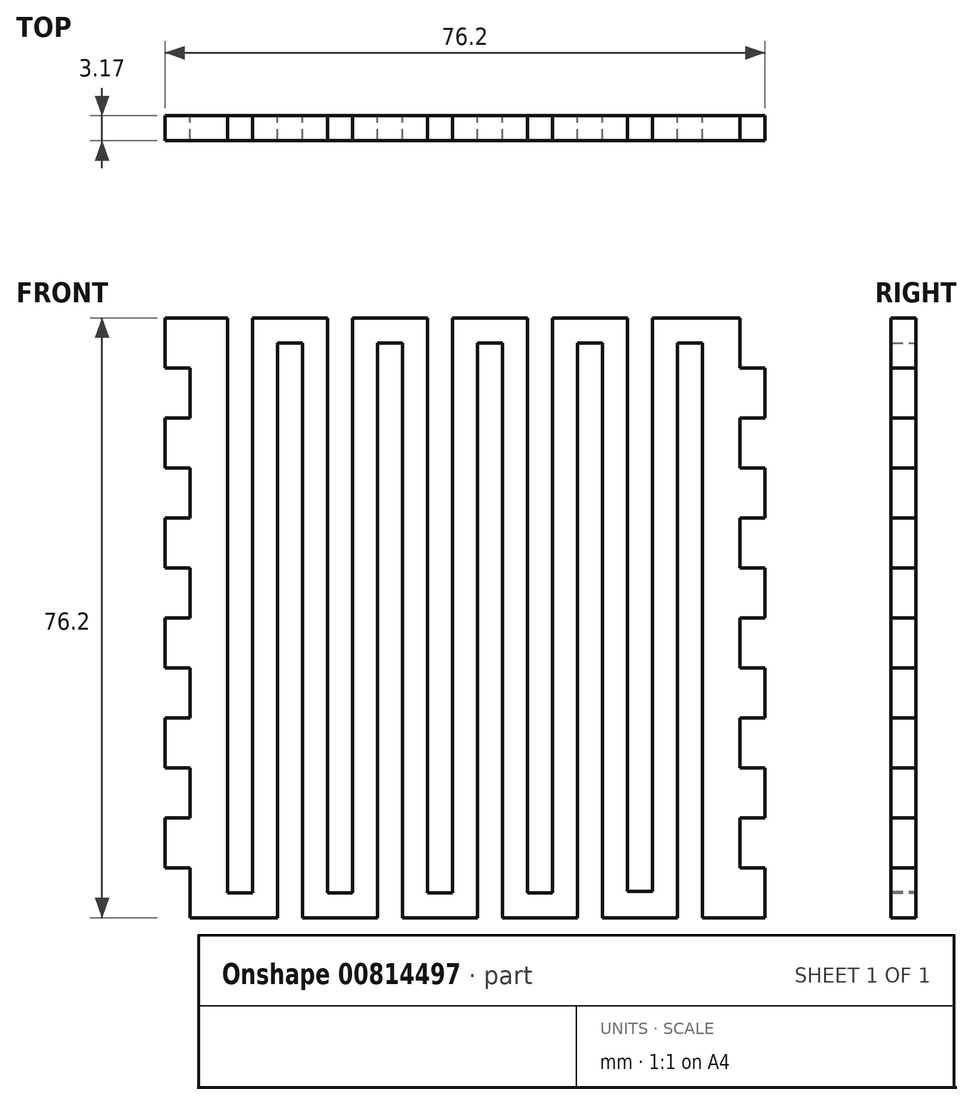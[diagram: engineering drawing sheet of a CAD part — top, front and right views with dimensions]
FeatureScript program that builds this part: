
annotation { "Feature Type Name" : "Feature", "Feature Type Description" : "" }
export const myFeature = defineFeature(function(context is Context, id is Id, definition is map)
    precondition{}
    {
        {
            var Q0;
            Q0=qCreatedBy(makeId("Front.planeOp"),FACE);
            var sketch = newSketch(context, id + "F0", { "sketchPlane" : qUnion([Q0])});
            skLineSegment(sketch, "E0.bottom", {"start": v(-38.1, 38.1) * mm, "end": v(38.1, 38.1) * mm});
            skLineSegment(sketch, "E0.top", {"start": v(-38.1, -38.1) * mm, "end": v(38.1, -38.1) * mm});
            skLineSegment(sketch, "E0.left", {"start": v(-38.1, 38.1) * mm, "end": v(-38.1, -38.1) * mm});
            skLineSegment(sketch, "E0.right", {"start": v(38.1, 38.1) * mm, "end": v(38.1, -38.1) * mm});
            skLineSegment(sketch, "E1.bottom", {"start": v(34.93, 38.1) * mm, "end": v(38.1, 38.1) * mm});
            skLineSegment(sketch, "E1.top", {"start": v(34.93, 31.75) * mm, "end": v(38.1, 31.75) * mm});
            skLineSegment(sketch, "E1.left", {"start": v(34.93, 38.1) * mm, "end": v(34.93, 31.75) * mm});
            skLineSegment(sketch, "E1.right", {"start": v(38.1, 38.1) * mm, "end": v(38.1, 31.75) * mm});
            skLineSegment(sketch, "E2.bottom", {"start": v(34.93, 25.4) * mm, "end": v(38.1, 25.4) * mm});
            skLineSegment(sketch, "E2.top", {"start": v(34.93, 19.05) * mm, "end": v(38.1, 19.05) * mm});
            skLineSegment(sketch, "E2.left", {"start": v(34.93, 25.4) * mm, "end": v(34.93, 19.05) * mm});
            skLineSegment(sketch, "E2.right", {"start": v(38.1, 25.4) * mm, "end": v(38.1, 19.05) * mm});
            skLineSegment(sketch, "E3.bottom", {"start": v(34.93, 12.7) * mm, "end": v(38.1, 12.7) * mm});
            skLineSegment(sketch, "E3.top", {"start": v(34.93, 6.35) * mm, "end": v(38.1, 6.35) * mm});
            skLineSegment(sketch, "E3.left", {"start": v(34.93, 12.7) * mm, "end": v(34.93, 6.35) * mm});
            skLineSegment(sketch, "E3.right", {"start": v(38.1, 12.7) * mm, "end": v(38.1, 6.35) * mm});
            skLineSegment(sketch, "E4.bottom", {"start": v(34.93, -12.7) * mm, "end": v(38.1, -12.7) * mm});
            skLineSegment(sketch, "E4.top", {"start": v(34.93, -19.05) * mm, "end": v(38.1, -19.05) * mm});
            skLineSegment(sketch, "E4.left", {"start": v(34.93, -12.7) * mm, "end": v(34.93, -19.05) * mm});
            skLineSegment(sketch, "E4.right", {"start": v(38.1, -12.7) * mm, "end": v(38.1, -19.05) * mm});
            skLineSegment(sketch, "E5.bottom", {"start": v(38.1, 0) * mm, "end": v(34.93, 0) * mm});
            skLineSegment(sketch, "E5.top", {"start": v(38.1, -6.35) * mm, "end": v(34.93, -6.35) * mm});
            skLineSegment(sketch, "E5.left", {"start": v(38.1, 0) * mm, "end": v(38.1, -6.35) * mm});
            skLineSegment(sketch, "E5.right", {"start": v(34.93, 0) * mm, "end": v(34.93, -6.35) * mm});
            skLineSegment(sketch, "E6.bottom", {"start": v(38.1, -25.4) * mm, "end": v(34.93, -25.4) * mm});
            skLineSegment(sketch, "E6.top", {"start": v(38.1, -31.75) * mm, "end": v(34.93, -31.75) * mm});
            skLineSegment(sketch, "E6.left", {"start": v(38.1, -25.4) * mm, "end": v(38.1, -31.75) * mm});
            skLineSegment(sketch, "E6.right", {"start": v(34.93, -25.4) * mm, "end": v(34.93, -31.75) * mm});
            skLineSegment(sketch, "E7.MirrorCS", {"start": v(-38.1, 12.7) * mm, "end": v(-38.1, 6.35) * mm});
            skLineSegment(sketch, "E8.MirrorCS", {"start": v(-38.1, -12.7) * mm, "end": v(-38.1, -19.05) * mm});
            skLineSegment(sketch, "E9.MirrorCS", {"start": v(-38.1, -25.4) * mm, "end": v(-38.1, -31.75) * mm});
            skLineSegment(sketch, "E10.MirrorCS", {"start": v(-38.1, 0) * mm, "end": v(-38.1, -6.35) * mm});
            skLineSegment(sketch, "E11.MirrorCS", {"start": v(-38.1, -31.75) * mm, "end": v(-34.93, -31.75) * mm});
            skLineSegment(sketch, "E12.MirrorCS", {"start": v(-34.93, -19.05) * mm, "end": v(-38.1, -19.05) * mm});
            skLineSegment(sketch, "E13.MirrorCS", {"start": v(-38.1, 38.1) * mm, "end": v(-38.1, 31.75) * mm});
            skLineSegment(sketch, "E14.MirrorCS", {"start": v(-34.93, 31.75) * mm, "end": v(-38.1, 31.75) * mm});
            skLineSegment(sketch, "E15.MirrorCS", {"start": v(-38.1, -6.35) * mm, "end": v(-34.93, -6.35) * mm});
            skLineSegment(sketch, "E16.MirrorCS", {"start": v(-34.93, 38.1) * mm, "end": v(-38.1, 38.1) * mm});
            skLineSegment(sketch, "E17.MirrorCS", {"start": v(-34.93, -12.7) * mm, "end": v(-38.1, -12.7) * mm});
            skLineSegment(sketch, "E18.MirrorCS", {"start": v(-38.1, 0) * mm, "end": v(-34.93, 0) * mm});
            skLineSegment(sketch, "E19.MirrorCS", {"start": v(-34.93, 12.7) * mm, "end": v(-38.1, 12.7) * mm});
            skLineSegment(sketch, "E20.MirrorCS", {"start": v(-38.1, 25.4) * mm, "end": v(-38.1, 19.05) * mm});
            skLineSegment(sketch, "E21.MirrorCS", {"start": v(-34.93, 6.35) * mm, "end": v(-38.1, 6.35) * mm});
            skLineSegment(sketch, "E22.MirrorCS", {"start": v(-34.93, 19.05) * mm, "end": v(-38.1, 19.05) * mm});
            skLineSegment(sketch, "E23.MirrorCS", {"start": v(-34.93, 25.4) * mm, "end": v(-38.1, 25.4) * mm});
            skLineSegment(sketch, "E24.MirrorCS", {"start": v(-38.1, -25.4) * mm, "end": v(-34.93, -25.4) * mm});
            skLineSegment(sketch, "E25", {"start": v(-34.93, 31.75) * mm, "end": v(-34.93, 25.4) * mm});
            skLineSegment(sketch, "E26", {"start": v(-34.93, 19.05) * mm, "end": v(-34.93, 12.7) * mm});
            skLineSegment(sketch, "E27", {"start": v(-34.93, 6.35) * mm, "end": v(-34.93, 0) * mm});
            skLineSegment(sketch, "E28", {"start": v(-34.93, -6.35) * mm, "end": v(-34.93, -12.7) * mm});
            skLineSegment(sketch, "E29", {"start": v(-34.93, -19.05) * mm, "end": v(-34.93, -25.4) * mm});
            skLineSegment(sketch, "E30", {"start": v(-34.93, -31.75) * mm, "end": v(-34.93, -38.1) * mm});
            skLineSegment(sketch, "E31.bottom", {"start": v(-30.16, 38.1) * mm, "end": v(-26.99, 38.1) * mm});
            skLineSegment(sketch, "E31.top", {"start": v(-30.16, -34.93) * mm, "end": v(-26.99, -34.93) * mm});
            skLineSegment(sketch, "E31.left", {"start": v(-30.16, 38.1) * mm, "end": v(-30.16, -34.93) * mm});
            skLineSegment(sketch, "E31.right", {"start": v(-26.99, 38.1) * mm, "end": v(-26.99, -34.93) * mm});
            skLineSegment(sketch, "E32.bottom", {"start": v(-23.81, -38.1) * mm, "end": v(-20.64, -38.1) * mm});
            skLineSegment(sketch, "E32.top", {"start": v(-23.81, 34.92) * mm, "end": v(-20.64, 34.92) * mm});
            skLineSegment(sketch, "E32.left", {"start": v(-23.81, -38.1) * mm, "end": v(-23.81, 34.92) * mm});
            skLineSegment(sketch, "E32.right", {"start": v(-20.64, -38.1) * mm, "end": v(-20.64, 34.92) * mm});
            skLineSegment(sketch, "E33.bottom", {"start": v(-14.29, 38.1) * mm, "end": v(-17.46, 38.1) * mm});
            skLineSegment(sketch, "E33.top", {"start": v(-14.29, -34.93) * mm, "end": v(-17.46, -34.93) * mm});
            skLineSegment(sketch, "E33.left", {"start": v(-14.29, 38.1) * mm, "end": v(-14.29, -34.93) * mm});
            skLineSegment(sketch, "E33.right", {"start": v(-17.46, 38.1) * mm, "end": v(-17.46, -34.93) * mm});
            skLineSegment(sketch, "E34.bottom", {"start": v(-11.11, -38.1) * mm, "end": v(-7.94, -38.1) * mm});
            skLineSegment(sketch, "E34.top", {"start": v(-11.11, 34.92) * mm, "end": v(-7.94, 34.92) * mm});
            skLineSegment(sketch, "E34.left", {"start": v(-11.11, -38.1) * mm, "end": v(-11.11, 34.92) * mm});
            skLineSegment(sketch, "E34.right", {"start": v(-7.94, -38.1) * mm, "end": v(-7.94, 34.92) * mm});
            skLineSegment(sketch, "E35.bottom", {"start": v(-1.59, 38.1) * mm, "end": v(-4.76, 38.1) * mm});
            skLineSegment(sketch, "E35.top", {"start": v(-1.59, -34.93) * mm, "end": v(-4.76, -34.93) * mm});
            skLineSegment(sketch, "E35.left", {"start": v(-1.59, 38.1) * mm, "end": v(-1.59, -34.93) * mm});
            skLineSegment(sketch, "E35.right", {"start": v(-4.76, 38.1) * mm, "end": v(-4.76, -34.93) * mm});
            skLineSegment(sketch, "E36.bottom", {"start": v(-3.25, -38.1) * mm, "end": v(-0.07, -38.1) * mm});
            skLineSegment(sketch, "E37.bottom", {"start": v(1.59, -38.1) * mm, "end": v(4.76, -38.1) * mm});
            skLineSegment(sketch, "E37.top", {"start": v(1.59, 34.93) * mm, "end": v(4.76, 34.93) * mm});
            skLineSegment(sketch, "E37.left", {"start": v(1.59, -38.1) * mm, "end": v(1.59, 34.93) * mm});
            skLineSegment(sketch, "E37.right", {"start": v(4.76, -38.1) * mm, "end": v(4.76, 34.93) * mm});
            skLineSegment(sketch, "E38.bottom", {"start": v(7.94, 38.1) * mm, "end": v(11.11, 38.1) * mm});
            skLineSegment(sketch, "E38.top", {"start": v(7.94, -34.92) * mm, "end": v(11.11, -34.92) * mm});
            skLineSegment(sketch, "E38.left", {"start": v(7.94, 38.1) * mm, "end": v(7.94, -34.92) * mm});
            skLineSegment(sketch, "E38.right", {"start": v(11.11, 38.1) * mm, "end": v(11.11, -34.92) * mm});
            skLineSegment(sketch, "E39.bottom", {"start": v(14.29, -38.1) * mm, "end": v(17.46, -38.1) * mm});
            skLineSegment(sketch, "E39.top", {"start": v(14.29, 34.93) * mm, "end": v(17.46, 34.93) * mm});
            skLineSegment(sketch, "E39.left", {"start": v(14.29, -38.1) * mm, "end": v(14.29, 34.93) * mm});
            skLineSegment(sketch, "E39.right", {"start": v(17.46, -38.1) * mm, "end": v(17.46, 34.93) * mm});
            skLineSegment(sketch, "E40.bottom", {"start": v(20.64, 38.1) * mm, "end": v(23.81, 38.1) * mm});
            skLineSegment(sketch, "E40.top", {"start": v(20.64, -34.75) * mm, "end": v(23.81, -34.75) * mm});
            skLineSegment(sketch, "E40.left", {"start": v(20.64, 38.1) * mm, "end": v(20.64, -34.75) * mm});
            skLineSegment(sketch, "E40.right", {"start": v(23.81, 38.1) * mm, "end": v(23.81, -34.75) * mm});
            skLineSegment(sketch, "E41.bottom", {"start": v(26.99, -38.1) * mm, "end": v(30.16, -38.1) * mm});
            skLineSegment(sketch, "E41.top", {"start": v(26.99, 34.93) * mm, "end": v(30.16, 34.93) * mm});
            skLineSegment(sketch, "E41.left", {"start": v(26.99, -38.1) * mm, "end": v(26.99, 34.93) * mm});
            skLineSegment(sketch, "E41.right", {"start": v(30.16, -38.1) * mm, "end": v(30.16, 34.93) * mm});
            skSolve(sketch);
        }
        {
            var Q0;
            {var subQ57=sQuery(id+"F0.wireOp",EDGE,"E1.top");Q0=makeQuery(id+"F0.imprint","IMPRINT",FACE,{"disambiguationData":[TD([[makeQuery(id+"F0.imprint","IMPRINT",EDGE,{"derivedFrom":subQ57}),-1.0]])]});}
            extrude(context, id + "F1", {"entities" : qUnion([Q0]), "depth" : 3.17 * mm, "offsetDistance" : 25.4 * mm});
        }
    });
